# Revit family: Shower_Set-DXV-Rem-D351007XX_Series
name_source: partatom
category: Plumbing Fixtures
units: mm (PartAtom-declared; Revit-internal decimal feet)

## family parameters
Cut with Voids When Loaded = No
Host = Face
OmniClass Number = 23.45.05.14.17
OmniClass Title = Showers
Part Type = Normal
Room Calculation Point = No
Round Connector Dimension = Use Radius
Shared = Yes

## types (4) — shared parameters
Assembly Code = D2010710
CW Connection = Yes
CWFU = 3
D35100781 - Hand Shower = Yes
Default Elevation = 48"
Description = Rem Personal Shower Set with Hand Shower
EPA WaterSense® Certified = Yes
HW Connection = Yes
HWFU = 3
Height = 27 3/8"
IAPMO Compliance = Meets or Exceeds ASME A112.18.1/CSA B125.1
Installation Type = Wall Mounted
Length = 2 1/8"
Manufacturer = DXV
Price = Prices may vary. Please consult Manufacturer Representative for most up-to-date price list.
Product Documentation Link = https://dxv01.blob.core.windows.net
Product Page URL = https://www.dxv.com
Tempered Water Connection Diameter = 1/2"
Tempered Water Connection Radius = 1/4"
URL = https://www.dxv.com
Vent Connection = No
WFU = 4
Warranty Documentation Link = https://www.dxv.com
Waste Connection = No
Width = 1"

## per-type parameters (varying)
| type | CEC Compliant | CalGreen Compliant | Finish | Flow Rate | Material |
| D35100780.100 | No | No | Metal-DXV-100-Polished Chrome | 2.0 GPM (7.6 L/min) | Metal-DXV-100-Polished Chrome |
| D35100780.144 | No | No | Metal-DXV-144-Brushed Nickel | 2.0 GPM (7.6 L/min) | Metal-DXV-144-Brushed Nickel |
| D3510079C.144 | Yes | Yes | Metal-DXV-144-Brushed Nickel | 1.8 gpm (6.8 L/min) | Metal-DXV-144-Brushed Nickel |
| D3510079C.100 | Yes | Yes | Metal-DXV-100-Polished Chrome | 1.8 gpm (6.8 L/min) | Metal-DXV-100-Polished Chrome |

note: column(s) folded — value = type name in every type: Model

## geometry (parser evidence)
native form markers: Sweep x2
no freeform markers — native parametric forms only
